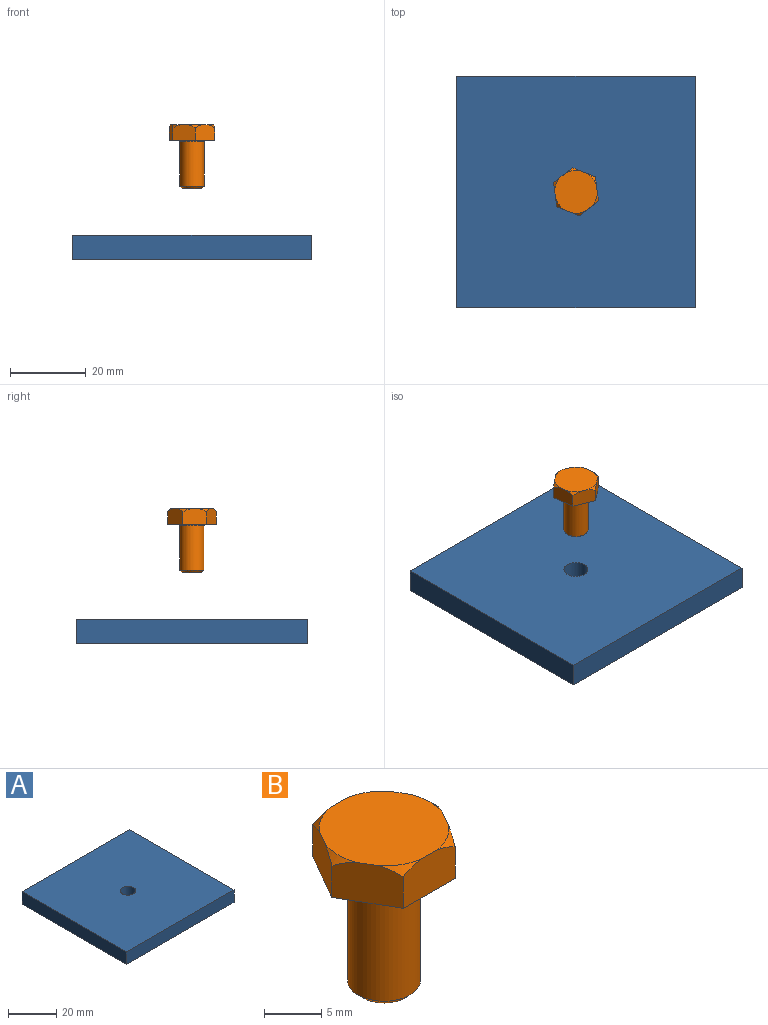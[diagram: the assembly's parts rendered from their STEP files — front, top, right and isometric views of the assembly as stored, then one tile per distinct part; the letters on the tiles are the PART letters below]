
ASSEMBLY  parts=2 mates=1
PART A: 7 faces, bbox 63x61.1x6.4 mm
  f0: plane 61.14x6.35mm, normal (1,0,0), area 388.2mm2, adj f1,f4,f5,f6
  f1: plane 62.96x6.35mm, normal (0,1,0), area 399.8mm2, adj f0,f2,f5,f6
  f2: plane 61.14x6.35mm, normal (-1,0,0), area 388.2mm2, adj f1,f4,f5,f6
  f3: cylinder r=3.17mm len=6.35mm, axis (0,0,1), area 126.7mm2, adj f5,f6
  f4: plane 62.96x6.35mm, normal (0,-1,0), area 399.8mm2, adj f0,f2,f5,f6
  f5: plane 62.96x61.14mm, normal (0,0,-1), area 3817.4mm2, adj f0,f1,f2,f3,f4
  f6: plane 62.96x61.14mm, normal (0,0,1), area 3817.4mm2, adj f0,f1,f2,f3,f4
PART B: 18 faces, bbox 12.9x12.6x16.8 mm
  f0: plane 5.08x5.08mm, normal (0,0,-1), area 20.3mm2, adj f17
  f1: cylinder r=3.17mm len=11.75mm, axis (0,0,-1), area 234.4mm2, adj f16,f17
  f2: plane 12.85x11.13mm, normal (0,0,-1), area 68.9mm2, adj f3,f4,f5,f6,f7,f8,f16
  f3: plane 5.57x4.14mm, normal (0.87,0.5,0), area 25.2mm2, adj f2,f4,f6,f9,f13,f15
  f4: plane 6.43x4.14mm, normal (0,1,0), area 25.2mm2, adj f2,f3,f5,f9,f14,f15
  f5: plane 5.57x4.14mm, normal (-0.87,0.5,0), area 25.2mm2, adj f2,f4,f7,f9,f12,f14
  f6: plane 5.57x4.14mm, normal (0.87,-0.5,0), area 25.2mm2, adj f2,f3,f8,f9,f11,f13
  f7: plane 5.57x4.14mm, normal (-0.87,-0.5,0), area 25.2mm2, adj f2,f5,f8,f9,f10,f12
  f8: plane 6.43x4.14mm, normal (0,-1,0), area 25.2mm2, adj f2,f6,f7,f9,f10,f11
  f9: plane 11.32x11.13mm, normal (0,0,1), area 99.9mm2, adj f3,f4,f5,f6,f7,f8,f10,f11
  f10: cone r=5.66mm half-angle=45deg, axis (0,0,-1), area 1.7mm2, adj f7,f8,f9
  f11: cone r=5.66mm half-angle=45deg, axis (0,0,-1), area 1.7mm2, adj f6,f8,f9
  f12: cone r=5.66mm half-angle=45deg, axis (0,0,-1), area 1.7mm2, adj f5,f7,f9
  f13: cone r=5.66mm half-angle=45deg, axis (0,0,-1), area 1.7mm2, adj f3,f6,f9
  f14: cone r=5.66mm half-angle=45deg, axis (0,0,-1), area 1.7mm2, adj f4,f5,f9
  f15: cone r=5.66mm half-angle=45deg, axis (0,0,-1), area 1.7mm2, adj f3,f4,f9
  f16: torus R=3.49mm, axis (0,0,1), area 10.3mm2, adj f1,f2
  f17: cone r=2.54mm half-angle=45deg, axis (0,0,1), area 16.1mm2, adj f0,f1
PLACE A at identity fixed
PLACE B rot(axis=(0,0,1),97.9deg) t=(0,0,-0.37)mm
MATE cylindrical B.f1 <-> A.f3  axis (0,0,1) through (0,0,25.03)mm
